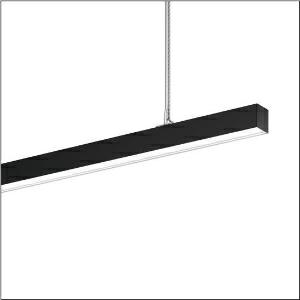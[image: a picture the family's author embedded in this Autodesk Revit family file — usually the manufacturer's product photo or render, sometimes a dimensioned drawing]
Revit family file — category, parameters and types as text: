
# Revit family: silica_r__21_51mx30tct9b_d278
name_source: partatom
category: Lighting Fixtures
units: mm (PartAtom-declared; Revit-internal decimal feet)

## family parameters
Cut with Voids When Loaded = No
Host = Face
Light Source = No
Part Type = Normal
Room Calculation Point = No
Round Connector Dimension = Use Diameter
Shared = No

## types (1)
- --- (1 x LED, 10300 lm, 84.4 W, 6500K)
    Apparent Load = 84 VA
    CIE Flux Codes = 47 79 96 58 100
    Color Rendering = 80
    Color Temperature = 6500K
    Default Elevation = 1800 mm
    Description = Silica® 21, office luminaire, primary optical cover: cover, of PMMA, opal, light emission: direct/indirect distribution, primary light characteristic: symmetric, installation type: suspended mounting, LED, rated luminous flux: 10.300lm, luminous efficacy: 116lm/W, light colour: 8tw, colour temperature: 2700..6500K, control gear: ECG DALI, with terminal, 3+2-pole, max. 2.5mm², mains connection: 220..240V, AC, 50/60Hz, rated input power: 88.7W, luminaire housing, of aluminium, jet black (RAL 9005), length: 3.004mm, width: 53mm, height: 53mm, protection rating (complete): IP20, insulation class (complete): insulation class I (protective earthing), certification: CE, permissible operating ambient temperature: 0..+35°C, standard: EN 50419, packaging unit: 1 piece
    Height = 53 mm
    Lamp = 1 x LED
    Lamp Light Flux = 10300 lm
    Lamp Power = 84.4 W
    Lamp count = 1
    Length = 3004 mm
    Luminous efficacy = 122 lm/W
    Manufacturer = Siteco
    ModVariant = No
    Model = 51MX30TCT9B
    Mounting Place = Ceiling
    Mounting Type = Pendant
    Number of Poles = 1
    OnlyDefault = Yes
    Power Factor = 1
    Product Name = Silica® 21
    Product group = office luminaire | ceiling pendant
    ProductGroupID = 902
    Protection Class = Protection class I
    Protection Degree = IP 20
    RLX_Detail_Level = 1
    RLX_Emergency_Light_Flux = 0 lm
    RLX_Emergency_Type = 0
    RLX_Emergency_Type_DB = No
    RlxData = <blob elided: 22769 chars, md5=08155edf>
    Socket = socket
    Standby Power = 0 W
    System Light Flux = 10300 lm
    System Power = 84 W
    Type Comments = individual setting
    Type Image = l_1335856.jpg
    URL = http://relux.com
    VarID = @adj_109429
    Voltage = 0 V
    Weight = 0.00 kg
    Width = 53 mm

## geometry (parser evidence)
native form markers: Blend x4, Sweep x10
no freeform markers — native parametric forms only
